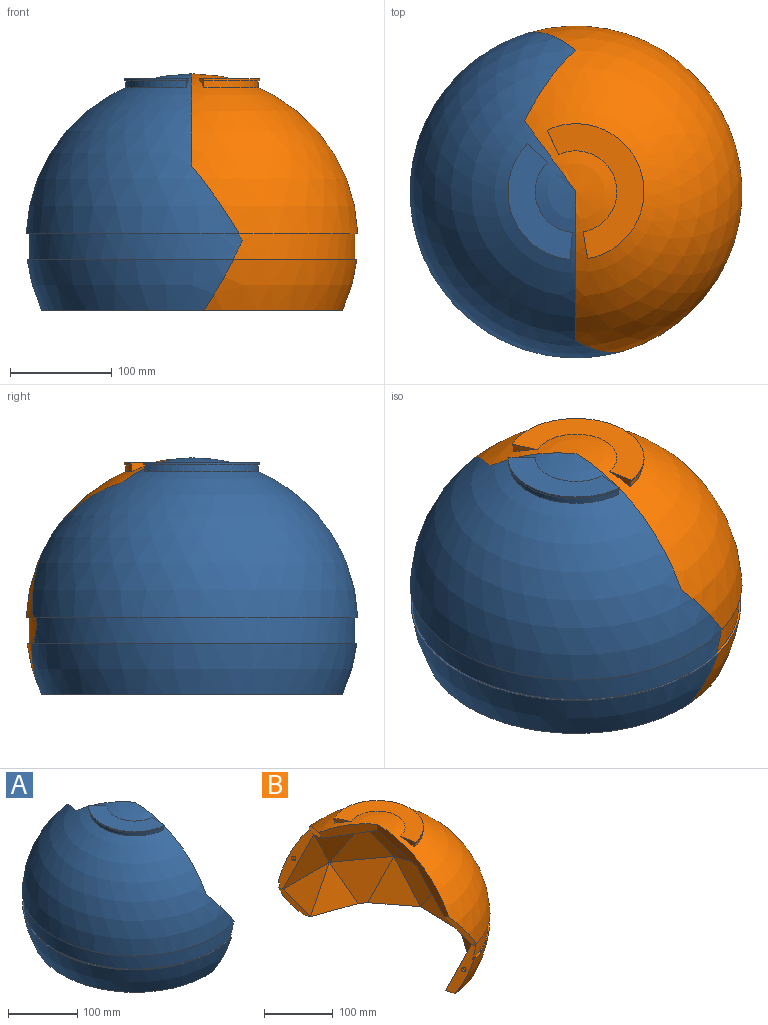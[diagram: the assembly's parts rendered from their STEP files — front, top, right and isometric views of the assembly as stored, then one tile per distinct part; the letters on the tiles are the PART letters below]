
ASSEMBLY  parts=2 mates=1
PART A: 52 faces, bbox 213x326.8x232.7 mm
  f0: cylinder r=3.17mm len=7.38mm, axis (-0.85,-0.28,0.45), area 76mm2, adj f5,f51
  f1: cylinder r=3.17mm len=7.38mm, axis (-0.85,-0.28,0.45), area 76mm2, adj f4,f50
  f2: sphere r=163.5mm, area 25822.1mm2, adj f5,f7,f9,f41
  f3: plane 73.23x49.54mm, normal (0.81,0.26,0.53), area 1205.2mm2, adj f5,f6,f10,f11,f42,f43
  f4: plane 86.11x49.54mm, normal (0.85,0.28,-0.45), area 1448.1mm2, adj f1,f6,f7,f18,f37,f42,f43
  f5: plane 68.59x42.47mm, normal (0.85,0.28,-0.45), area 1157.8mm2, adj f0,f2,f3,f8,f9,f41,f42
  f6: sphere r=163.5mm, area 72868.1mm2, adj f3,f4,f11,f17,f18,f43,f44,f47
  f7: plane 68.59x49.56mm, normal (0.81,0.26,0.53), area 1114.5mm2, adj f2,f4,f9,f40,f41,f42
  f8: plane 94.78x68.58mm, normal (0,0.98,0.19), area 3802.7mm2, adj f5,f9,f10,f39
  f9: plane 296.3x160.1mm, normal (0,0,-1), area 7470.9mm2, adj f2,f5,f7,f8,f32,f33,f34,f35
  f10: plane 94.78x68.58mm, normal (0,0.99,-0.13), area 3275.8mm2, adj f3,f8,f16
  f11: plane 146.46x95.48mm, normal (1,0,0), area 2517mm2, adj f3,f6,f13,f15,f17
  f12: plane 90.14x76.67mm, normal (0.32,-0.1,-0.94), area 3275.8mm2, adj f13,f17,f30
  f13: plane 80.62x76.67mm, normal (0.19,0.27,-0.94), area 3275.8mm2, adj f11,f12,f14
  f14: plane 80.62x76.67mm, normal (0.36,0.49,-0.79), area 3889.5mm2, adj f13,f15,f31
  f15: plane 76.67x61.87mm, normal (0.19,0.72,-0.66), area 3275.8mm2, adj f11,f14,f16
  f16: plane 80.62x76.67mm, normal (0.32,0.89,-0.33), area 3275.8mm2, adj f10,f15,f29
  f17: plane 69.74x50.67mm, normal (0.81,0.59,0), area 1265.7mm2, adj f6,f11,f12,f18
  f18: plane 74.11x58.87mm, normal (0.85,-0.28,0.45), area 1527.9mm2, adj f4,f6,f17,f38
  f19: plane 82.7x80.62mm, normal (0.94,-0.02,-0.33), area 3275.8mm2, adj f20,f22,f24
  f20: plane 90.14x80.62mm, normal (0.93,-0.3,-0.19), area 3889.5mm2, adj f19,f21,f25
  f21: plane 80.62x70.65mm, normal (0.78,-0.53,-0.33), area 3275.8mm2, adj f20,f26,f27
  f22: plane 82.7x61.87mm, normal (0.75,0.04,-0.66), area 3275.8mm2, adj f19,f30,f31
  f23: plane 80.62x63.15mm, normal (0.75,0.57,-0.33), area 3275.8mm2, adj f24,f29,f31
  f24: plane 90.14x68.58mm, normal (0.94,0.31,-0.13), area 3275.8mm2, adj f19,f23,f33
  f25: plane 90.14x68.58mm, normal (0.94,-0.31,0.13), area 3275.8mm2, adj f20,f34,f35
  f26: plane 76.67x68.58mm, normal (0.58,-0.8,-0.13), area 3275.8mm2, adj f21,f36,f37
  f27: plane 76.67x70.65mm, normal (0.58,-0.47,-0.66), area 3275.8mm2, adj f21,f30,f38
  f28: plane 76.67x68.58mm, normal (0.58,0.8,0.13), area 3275.8mm2, adj f29,f32,f39
  f29: plane 80.62x76.67mm, normal (0.58,0.79,-0.19), area 3889.5mm2, adj f16,f23,f28
  f30: plane 90.14x76.67mm, normal (0.58,-0.19,-0.79), area 3889.5mm2, adj f12,f22,f27
  f31: plane 80.62x61.87mm, normal (0.63,0.41,-0.66), area 3275.8mm2, adj f14,f22,f23
  f32: plane 68.58x63.21mm, normal (0.78,0.53,0.33), area 2786.6mm2, adj f9,f28,f33
  f33: plane 90.14x68.58mm, normal (0.93,0.3,0.19), area 3802.7mm2, adj f9,f24,f32,f34
  f34: plane 76.67x68.58mm, normal (0.94,0.02,0.33), area 2786.6mm2, adj f9,f25,f33
  f35: plane 68.58x60.85mm, normal (0.75,-0.57,0.33), area 2786.6mm2, adj f9,f25,f36
  f36: plane 76.67x68.58mm, normal (0.58,-0.79,0.19), area 3802.7mm2, adj f9,f26,f35,f40
  f37: plane 80.62x80.62mm, normal (0.27,-0.9,-0.33), area 3275.8mm2, adj f4,f26,f38
  f38: plane 80.62x65.22mm, normal (0.27,-0.7,-0.66), area 3275.8mm2, adj f18,f27,f37
  f39: plane 73.54x68.58mm, normal (0.27,0.9,0.33), area 2786.6mm2, adj f8,f9,f28
  f40: plane 72.3x68.58mm, normal (0.32,-0.89,0.33), area 2786.6mm2, adj f7,f9,f36
  f41: plane 319.95x203.47mm, normal (0,0,1), area 1030.1mm2, adj f2,f5,f7,f42
  f42: cylinder r=160.33mm len=316mm, axis (0,0,-1), area 12811.9mm2, adj f3,f4,f5,f7,f41,f43
  f43: plane 319.77x210.02mm, normal (0,0,-1), area 1557.8mm2, adj f3,f4,f6,f42
  f44: cylinder r=65.43mm len=111.44mm, axis (0,0,1), area 985.2mm2, adj f6,f45,f48,f49
  f45: plane 114.04x61.25mm, normal (0,0,-1), area 228.9mm2, adj f44,f46,f48,f49
  f46: cylinder r=66.95mm len=114.04mm, axis (0,0,1), area 303.7mm2, adj f45,f47,f48,f49
  f47: plane 114.04x63.45mm, normal (0,0,1), area 3249.5mm2, adj f6,f46,f48,f49
  f48: plane 18.9x18.9mm, normal (0.71,0.71,0), area 102.2mm2, adj f6,f44,f45,f46,f47
  f49: plane 26.62x8.64mm, normal (1,-0.09,0), area 102.2mm2, adj f6,f44,f45,f46,f47
  f50: plane 6.1x5.68mm, normal (0.85,0.28,-0.45), area 31.7mm2, adj f1
  f51: plane 6.1x5.68mm, normal (0.85,0.28,-0.45), area 31.7mm2, adj f0
PART B: 54 faces, bbox 259.4x326.8x232.7 mm
  f0: sphere r=163.5mm, area 25272mm2, adj f3,f5,f6,f42
  f1: plane 86.11x49.54mm, normal (-0.85,-0.28,0.45), area 1443.4mm2, adj f4,f5,f10,f37,f41,f43,f52
  f2: plane 73.23x49.54mm, normal (-0.81,-0.26,-0.53), area 1205.2mm2, adj f3,f4,f32,f35,f41,f43
  f3: plane 68.59x42.47mm, normal (-0.85,-0.28,0.45), area 1153.1mm2, adj f0,f2,f6,f24,f42,f43,f51
  f4: sphere r=163.5mm, area 80930.3mm2, adj f1,f2,f35,f36,f37,f41,f44,f47
  f5: plane 68.59x49.56mm, normal (-0.81,-0.26,-0.53), area 1114.5mm2, adj f0,f1,f6,f11,f42,f43
  f6: plane 295.86x151.73mm, normal (0,0,-1), area 7218.5mm2, adj f0,f3,f5,f16,f17,f18,f19,f20
  f7: plane 90.14x80.62mm, normal (-0.93,-0.3,-0.19), area 3889.5mm2, adj f8,f13,f14
  f8: plane 90.14x68.58mm, normal (-0.94,-0.31,0.13), area 3275.8mm2, adj f7,f18,f19
  f9: plane 76.67x68.58mm, normal (-0.58,-0.8,-0.13), area 3275.8mm2, adj f12,f13,f17
  f10: plane 94.78x80.62mm, normal (0,-0.98,-0.19), area 3889.5mm2, adj f1,f11,f12
  f11: plane 94.78x68.58mm, normal (0,-0.99,0.13), area 3275.8mm2, adj f5,f10,f16
  f12: plane 80.62x80.62mm, normal (-0.27,-0.9,-0.33), area 3275.8mm2, adj f9,f10,f22
  f13: plane 80.62x70.65mm, normal (-0.78,-0.53,-0.33), area 3275.8mm2, adj f7,f9,f23
  f14: plane 82.7x80.62mm, normal (-0.94,-0.02,-0.33), area 3275.8mm2, adj f7,f15,f26
  f15: plane 90.14x68.58mm, normal (-0.94,0.31,-0.13), area 3275.8mm2, adj f14,f20,f27
  f16: plane 72.3x68.58mm, normal (-0.32,-0.89,0.33), area 2786.6mm2, adj f6,f11,f17
  f17: plane 76.67x68.58mm, normal (-0.58,-0.79,0.19), area 3802.7mm2, adj f6,f9,f16,f18
  f18: plane 68.58x60.85mm, normal (-0.75,-0.57,0.33), area 2786.6mm2, adj f6,f8,f17
  f19: plane 76.67x68.58mm, normal (-0.94,0.02,0.33), area 2786.6mm2, adj f6,f8,f20
  f20: plane 90.14x68.58mm, normal (-0.93,0.3,0.19), area 3802.7mm2, adj f6,f15,f19,f21
  f21: plane 68.58x63.21mm, normal (-0.78,0.53,0.33), area 2786.6mm2, adj f6,f20,f25
  f22: plane 80.62x65.22mm, normal (-0.27,-0.7,-0.66), area 3275.8mm2, adj f12,f23,f38
  f23: plane 76.67x70.65mm, normal (-0.58,-0.47,-0.66), area 3275.8mm2, adj f13,f22,f28
  f24: plane 73.54x68.58mm, normal (-0.27,0.9,0.33), area 2786.6mm2, adj f3,f6,f25
  f25: plane 76.67x68.58mm, normal (-0.58,0.8,0.13), area 3275.8mm2, adj f21,f24,f29
  f26: plane 82.7x61.87mm, normal (-0.75,0.04,-0.66), area 3275.8mm2, adj f14,f28,f30
  f27: plane 80.62x63.15mm, normal (-0.75,0.57,-0.33), area 3275.8mm2, adj f15,f29,f30
  f28: plane 90.14x76.67mm, normal (-0.58,-0.19,-0.79), area 3889.5mm2, adj f23,f26,f34
  f29: plane 80.62x76.67mm, normal (-0.58,0.79,-0.19), area 3889.5mm2, adj f25,f27,f32
  f30: plane 80.62x61.87mm, normal (-0.63,0.41,-0.66), area 3275.8mm2, adj f26,f27,f40
  f31: plane 94.78x65.22mm, normal (0,-0.33,-0.94), area 3275.8mm2, adj f34,f36,f38
  f32: plane 80.62x76.67mm, normal (-0.32,0.89,-0.33), area 3275.8mm2, adj f2,f29,f33
  f33: plane 76.67x61.87mm, normal (-0.19,0.72,-0.66), area 3275.8mm2, adj f32,f35,f40
  f34: plane 90.14x76.67mm, normal (-0.32,-0.1,-0.94), area 3275.8mm2, adj f28,f31,f39
  f35: plane 146.46x95.48mm, normal (-1,0,0), area 2517mm2, adj f2,f4,f33,f36,f39
  f36: plane 69.74x50.67mm, normal (-0.81,-0.59,0), area 1265.7mm2, adj f4,f31,f35,f37
  f37: plane 74.11x58.87mm, normal (-0.85,0.28,-0.45), area 1527.9mm2, adj f1,f4,f36,f38
  f38: plane 94.78x65.22mm, normal (0,-0.61,-0.79), area 3889.5mm2, adj f22,f31,f37
  f39: plane 80.62x76.67mm, normal (-0.19,0.27,-0.94), area 3275.8mm2, adj f34,f35,f40
  f40: plane 80.62x76.67mm, normal (-0.36,0.49,-0.79), area 3889.5mm2, adj f30,f33,f39
  f41: plane 320x210.76mm, normal (0,0,-1), area 1562.6mm2, adj f1,f2,f4,f43
  f42: plane 319.4x201.31mm, normal (0,0,1), area 1021.1mm2, adj f0,f3,f5,f43
  f43: cylinder r=160.33mm len=315.45mm, axis (0,0,-1), area 12775mm2, adj f1,f2,f3,f5,f41,f42
  f44: cylinder r=65.43mm len=129.86mm, axis (0,0,1), area 1477.8mm2, adj f4,f45,f48,f49
  f45: plane 132.89x95.25mm, normal (0,0,-1), area 343.3mm2, adj f44,f46,f48,f49
  f46: cylinder r=66.95mm len=132.89mm, axis (0,0,1), area 455.6mm2, adj f45,f47,f48,f49
  f47: plane 132.89x95.25mm, normal (0,0,1), area 4874.2mm2, adj f4,f46,f48,f49
  f48: plane 26.32x8.64mm, normal (-0.98,-0.17,0), area 102.2mm2, adj f4,f44,f45,f46,f47
  f49: plane 24.22x11.29mm, normal (-0.91,-0.42,0), area 102.2mm2, adj f4,f44,f45,f46,f47
  f50: plane 6.54x6.09mm, normal (-0.85,-0.28,0.45), area 36.4mm2, adj f51
  f51: cylinder r=3.4mm len=9.18mm, axis (-0.85,-0.28,0.45), area 140.7mm2, adj f3,f50
  f52: cylinder r=3.4mm len=9.18mm, axis (-0.85,-0.28,0.45), area 140.7mm2, adj f1,f53
  f53: plane 6.54x6.09mm, normal (-0.85,-0.28,0.45), area 36.4mm2, adj f52
PLACE A t=(-723.75,-221.84,177.7)mm
PLACE B t=(-723.75,-221.84,177.7)mm
MATE fastened A.f18 <-> B.f37  axis (0.85,-0.28,0.45) through (-748.79,-118.72,357.65)mm
